# Revit family: 1 SOUND_Tower_Rigging System Mounted
name_source: partatom
category: Communication Devices
units: mm (PartAtom-declared; Revit-internal decimal feet)

## family parameters
Always vertical = No
Cut with Voids When Loaded = No
Maintain Annotation Orientation = No
Part Type = Normal
Room Calculation Point = No
Round Connector Dimension = Use Diameter
Shared = No
Work Plane-Based = Yes

## types (3) — shared parameters
Accessory Used = Tower Rigging System
Category = Speaker
Construction = Finland birch plywood (phenolic glue), polyurea, clear matte salt and UV resistant coating, 316 stainless steel hardware, 3D spacer mesh fabric
Default Elevation = 0.00 mm
Manufacturer = 1 Sound
Rigging = Proprietary rigging elements and fly bars -3 deg, 0 deg, +3 deg, +6 deg, +9 deg; (14) available M6 points
URL = https://www.1-sound.com

## per-type parameters (varying)
| type | Bandwidth | Connectors | Dimensions (HxWxD) | Impedance | Model | Power | Rigging Height | Speaker Height | Weight |
| Tower LCC44 | 105 Hz - 18 kHz (-6 dB) | (4) NL4, 1+1-front speakers, 2+2-rear speakers, each allowing for audio inputs and linking | 452.00mm x 160.00mm x 240.00mm | 16Ω front speakers, 24Ω rear speakers | LCC44 | 800 watts front + 400 watts rear (continuous), 400 watts + 200 watts (AES) | 480.20 mm | 452.00 mm | 22 lbs / 10 kg |
| Tower LCC84 | 105 Hz - 18 kHz (-6 dB) | (4) NL4, 1+1-front speakers, 2+2-rear speakers, each allowing for audio inputs and linking | 878.00mm x 160.00mm x 240.00mm | 8Ω front speakers, 12Ω rear speakers | LCC84 | 1600 watts front + 800 watts rear (continuous), 800 watts + 400 watts (AES) | 906.20 mm | 878.00 mm | 43 lbs / 19.5 kg |
| Tower LF44 | 70 Hz - 200 Hz (-6 dB preset depending) | (4) NL4, each allowing for audio inputs and linking, (3) Neutrik NDL dummyPLUGs | 452.00mm x 160.00mm x 240.00mm | 8Ω | LF44 | 560 watts (program), 280 watts (AES) | 480.20 mm | 452.00 mm | 17 lbs / 7.7kg |

## geometry (parser evidence)
native form markers: Sweep x13
no freeform markers — native parametric forms only
